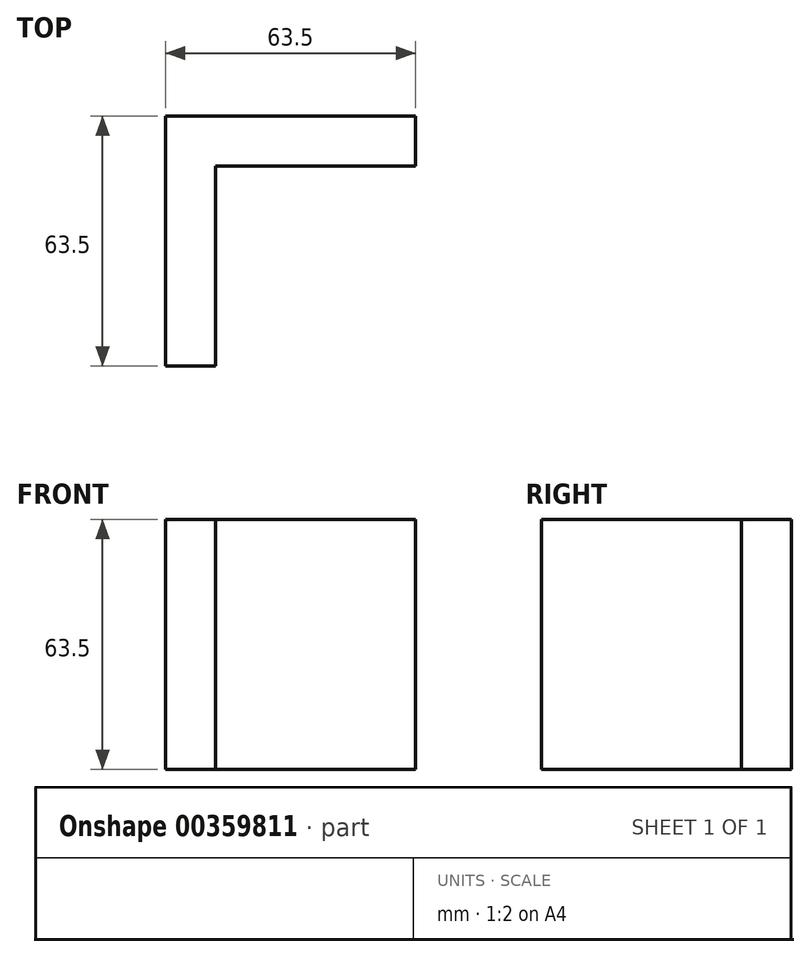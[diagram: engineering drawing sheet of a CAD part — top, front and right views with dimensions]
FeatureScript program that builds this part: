
annotation { "Feature Type Name" : "Feature", "Feature Type Description" : "" }
export const myFeature = defineFeature(function(context is Context, id is Id, definition is map)
    precondition{}
    {
        {
            var Q0;
            Q0=qCreatedBy(makeId("Front.planeOp"),FACE);
            var sketch = newSketch(context, id + "F0", { "sketchPlane" : qUnion([Q0])});
            skLineSegment(sketch, "E0.bottom", {"start": v(0, 0) * mm, "end": v(12.7, 0) * mm});
            skLineSegment(sketch, "E0.top", {"start": v(0, -63.5) * mm, "end": v(12.7, -63.5) * mm});
            skLineSegment(sketch, "E0.left", {"start": v(0, 0) * mm, "end": v(0, -63.5) * mm});
            skLineSegment(sketch, "E0.right", {"start": v(12.7, 0) * mm, "end": v(12.7, -63.5) * mm});
            skSolve(sketch);
        }
        {
            var Q0;
            Q0 = qSketchRegion(id + "F0", true);
            extrude(context, id + "F1", {"entities" : qUnion([Q0]), "depth" : 63.5 * mm});
        }
        {
            var Q0;
            Q0=qCreatedBy(makeId("Right.planeOp"),FACE);
            var sketch = newSketch(context, id + "F2", { "sketchPlane" : qUnion([Q0])});
            skLineSegment(sketch, "E1.bottom", {"start": v(0, 0) * mm, "end": v(-12.7, 0) * mm});
            skLineSegment(sketch, "E1.top", {"start": v(0, -63.5) * mm, "end": v(-12.7, -63.5) * mm});
            skLineSegment(sketch, "E1.left", {"start": v(0, 0) * mm, "end": v(0, -63.5) * mm});
            skLineSegment(sketch, "E1.right", {"start": v(-12.7, 0) * mm, "end": v(-12.7, -63.5) * mm});
            skSolve(sketch);
        }
        {
            var Q0;
            Q0=makeQuery(id+"F2.imprint","IMPRINT",FACE,{"disambiguationData":[TD([[makeQuery(id+"F2.imprint","IMPRINT",EDGE,{"derivedFrom":sQuery(id+"F2.wireOp",EDGE,"E1.bottom")}),1.0]])]});
            extrude(context, id + "F3", {"entities" : qUnion([Q0]), "operationType" : NewBodyOperationType.ADD, "depth" : 63.5 * mm});
        }
    });
